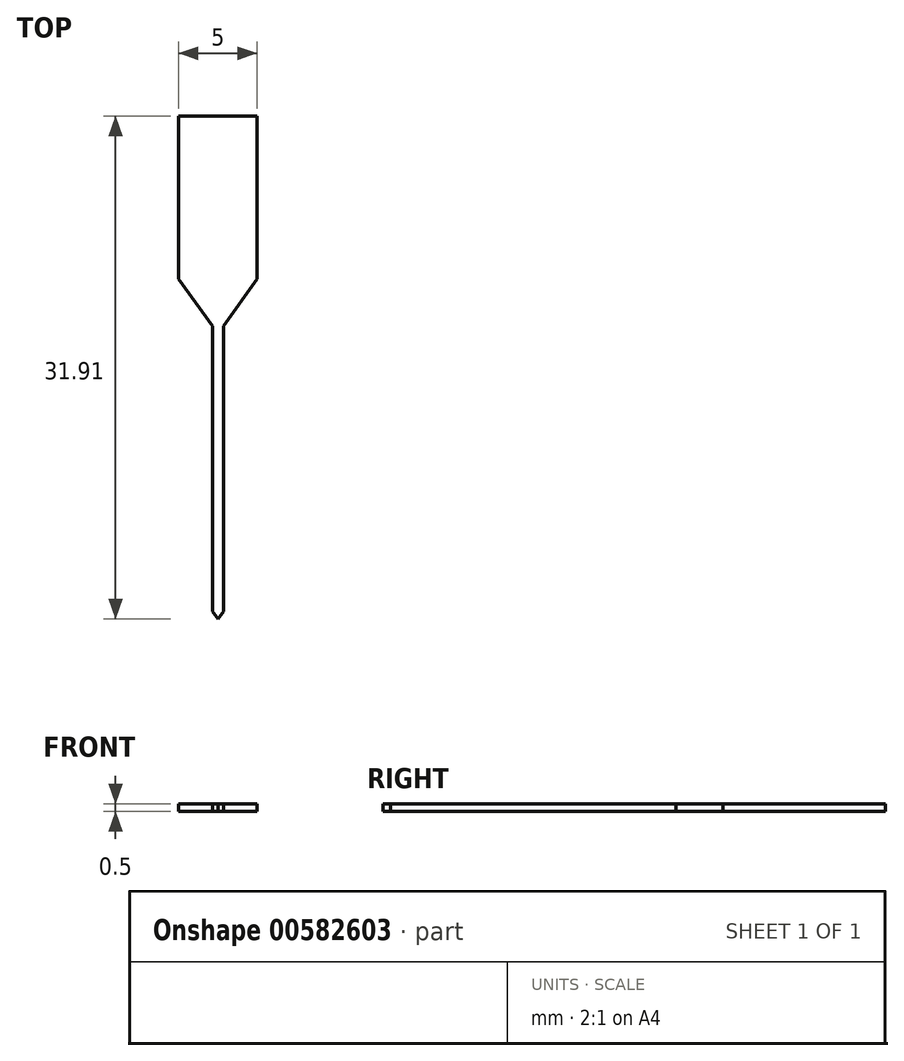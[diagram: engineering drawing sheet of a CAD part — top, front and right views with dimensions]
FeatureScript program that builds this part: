
annotation { "Feature Type Name" : "Feature", "Feature Type Description" : "" }
export const myFeature = defineFeature(function(context is Context, id is Id, definition is map)
    precondition{}
    {
        {
            var Q0;
            Q0=qCreatedBy(makeId("Top.planeOp"),FACE);
            var sketch = newSketch(context, id + "F0", { "sketchPlane" : qUnion([Q0])});
            skLineSegment(sketch, "E0", {"start": v(0, 0) * mm, "end": v(2.5, 0) * mm});
            skLineSegment(sketch, "E1", {"start": v(2.5, 0) * mm, "end": v(2.5, -10.34) * mm});
            skLineSegment(sketch, "E2", {"start": v(2.5, -10.34) * mm, "end": v(0.35, -13.32) * mm});
            skLineSegment(sketch, "E3", {"start": v(0.35, -13.32) * mm, "end": v(0.35, -31.46) * mm});
            skLineSegment(sketch, "E4", {"start": v(0.35, -31.46) * mm, "end": v(0, -31.91) * mm});
            skLineSegment(sketch, "E5.MirrorCS", {"start": v(0, 0) * mm, "end": v(-2.5, 0) * mm});
            skLineSegment(sketch, "E6.MirrorCS", {"start": v(-2.5, 0) * mm, "end": v(-2.5, -10.34) * mm});
            skLineSegment(sketch, "E7.MirrorCS", {"start": v(-2.5, -10.34) * mm, "end": v(-0.35, -13.32) * mm});
            skLineSegment(sketch, "E8.MirrorCS", {"start": v(-0.35, -13.32) * mm, "end": v(-0.35, -31.46) * mm});
            skLineSegment(sketch, "E9.MirrorCS", {"start": v(-0.35, -31.46) * mm, "end": v(0, -31.91) * mm});
            skSolve(sketch);
        }
        {
            var Q0;
            Q0 = qSketchRegion(id + "F0", true);
            extrude(context, id + "F1", {"entities" : qUnion([Q0]), "depth" : 0.5 * mm, "offsetDistance" : 25 * mm});
        }
    });
